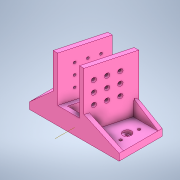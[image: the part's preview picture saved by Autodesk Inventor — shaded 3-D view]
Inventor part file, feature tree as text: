
AUTODESK INVENTOR PART (.ipt)
format: ipt  version: 2022.1 (Build 261234020, 234B)  size: 439,808 bytes
history: native  units: mm
features: sketch x21, extrude x12, hole x4, loft x4, split x1, plane x1, projected_geometry x1
ambient origin geometry x8: Origin, YZ Plane, XZ Plane, XY Plane, X Axis, Y Axis, Z Axis, Center Point
bodies: Body1 (feature_tree)
feature tree (44):
  extrude  "Extrusion8"  Depth=166.0mm
  extrude  "armsForCameraCase"  TaperAngle=0.0deg  [1 undecoded]
  extrude  "Extrusion10"  Depth=8.0mm
  extrude  "Extrusion11"  Depth=125.0mm TaperAngle=0.0deg
  extrude  "Extrusion12"  Depth=8.0mm
  hole  "Hole1"  [1 undecoded]
  extrude  "Extrusion13"  Depth=104.1375mm
  hole  "HoleForLeftSideOf2x4"  [1 undecoded]
  hole  "HolesForRightSideOf2x4"  [1 undecoded]
  extrude  "Extrusion14"  TaperAngle=0.0deg  [1 undecoded]
  extrude  "Extrusion15"  Depth=21.283555mm
  extrude  "Extrusion16"  Depth=30.0mm
  loft  "Loft5"
  loft  "Loft6"
  loft  "Loft7"
  loft  "Loft8"
  split  "Split3"
  extrude  "ExtrusionForMatingToLowerHalf"  TaperAngle=0.0deg  [1 undecoded]
  hole  "Hole5"  [1 undecoded]
  plane  "Work Plane3"
  sketch  "SketchForHoleToSupportCase"  dims[d110=0.0mm d111=0.0mm d112=8.0mm d113=16.0mm d114=8.0mm d115=8.0mm d116=0.0mm d117=0.0mm d152=30.0mm d153=30.0mm d154=0.0mm d155=90.0deg d156=0.0mm d157=90.0deg d158=30.0mm d159=30.0mm d160=0.0mm d161=90.0deg d162=0.0mm d163=90.0deg d164=39.0mm d165=30.0mm d166=0.0mm d167=90.0deg d168=0.0mm d169=90.0deg d170=30.0mm d171=30.0mm d172=0.0mm d173=90.0deg d174=0.0mm d175=90.0deg d191=12.5mm d192=0.0mm d195=5.1054mm d196=6.0mm d197=4.0mm d198=2.0mm d199=90.0deg d200=8.0mm d201=0.0mm d202=20.0mm d203=20.0mm d204=20.0mm d205=20.0mm d206=27.925268mm d208=30.0mm d209=5.1054mm d210=25.0mm d211=25.0mm d212=30.0mm d213=0.0mm d214=15.0mm d215=14.0mm d216=0.0mm d217=52.0mm d218=126.0mm d219=34.0mm d73=0.0625mm]
  extrude  "ExtrusionFor10Screw"  Depth=8.0mm
  extrude  "ExtrusionForWasher"  Depth=12.5mm
  sketch  "Sketch8"  dims[d28=80.0mm d29=166.0mm]
  sketch  "Sketch9"  dims[d30=8.0mm d31=0.0mm]
  sketch  "Sketch10"  dims[d32=8.0mm d33=8.0mm]
  sketch  "Sketch11"  dims[d34=140.0mm d35=0.0mm d37=125.0mm d38=0.0mm]
  sketch  "Sketch12"  dims[d39=-2.617994mm d40=8.0mm]
  sketch  "Sketch13"  dims[d42=8.0mm d44=20.32mm]
  sketch  "Sketch14"  dims[d45=20.32mm d46=104.1375mm]
  sketch  "Sketch15"  dims[d47=0.0mm d48=3.490659mm]
  sketch  "Sketch16"  dims[d49=20.0mm d50=0.0mm d51=90.0mm]
  sketch  "Sketch17"  dims[d52=6.7564mm d53=6.0mm d54=15.875mm d55=4.826mm d56=14.3117mm d57=8.0mm d58=20.594885mm d59=0.0mm d60=0.0mm]
  sketch  "Sketch18"  dims[d62=21.283555mm d63=21.283555mm]
  projected_geometry  "Projected Loop3"
  sketch  "Sketch19"  dims[d64=15.0mm]
  sketch  "Sketch27"  dims[d65=4.496mm d66=6.0mm d67=8.433mm d68=2.794mm d69=14.3117mm d70=8.0mm d71=0.0mm d72=30.0mm d74=20.0mm d75=30.0mm d77=20.0mm]
  sketch  "Sketch28"  dims[d80=20.0mm d81=15.0mm]
  sketch  "Sketch31"  dims[d82=30.0mm d84=20.0mm d85=30.0mm d87=20.0mm d90=20.0mm]
  sketch  "Sketch32"  dims[d91=4.496mm d92=6.0mm d93=8.433mm d94=2.0mm d95=14.3117mm d96=8.0mm d97=0.0mm d98=8.0mm]
  sketch  "Sketch33"  dims[d99=8.0mm d101=8.0mm]
  sketch  "Sketch34"  dims[d102=8.0mm d103=0.0mm d104=0.0mm]
  sketch  "Sketch40"  dims[d105=8.0mm d107=8.0mm]
  sketch  "Sketch42"  dims[d108=16.0mm d109=8.0mm]
note: 7 required parameter values undecoded (feature->parameter linkage not recoverable at this tier; creation-order binding heuristic only, values carry confidence <= 0.55)
